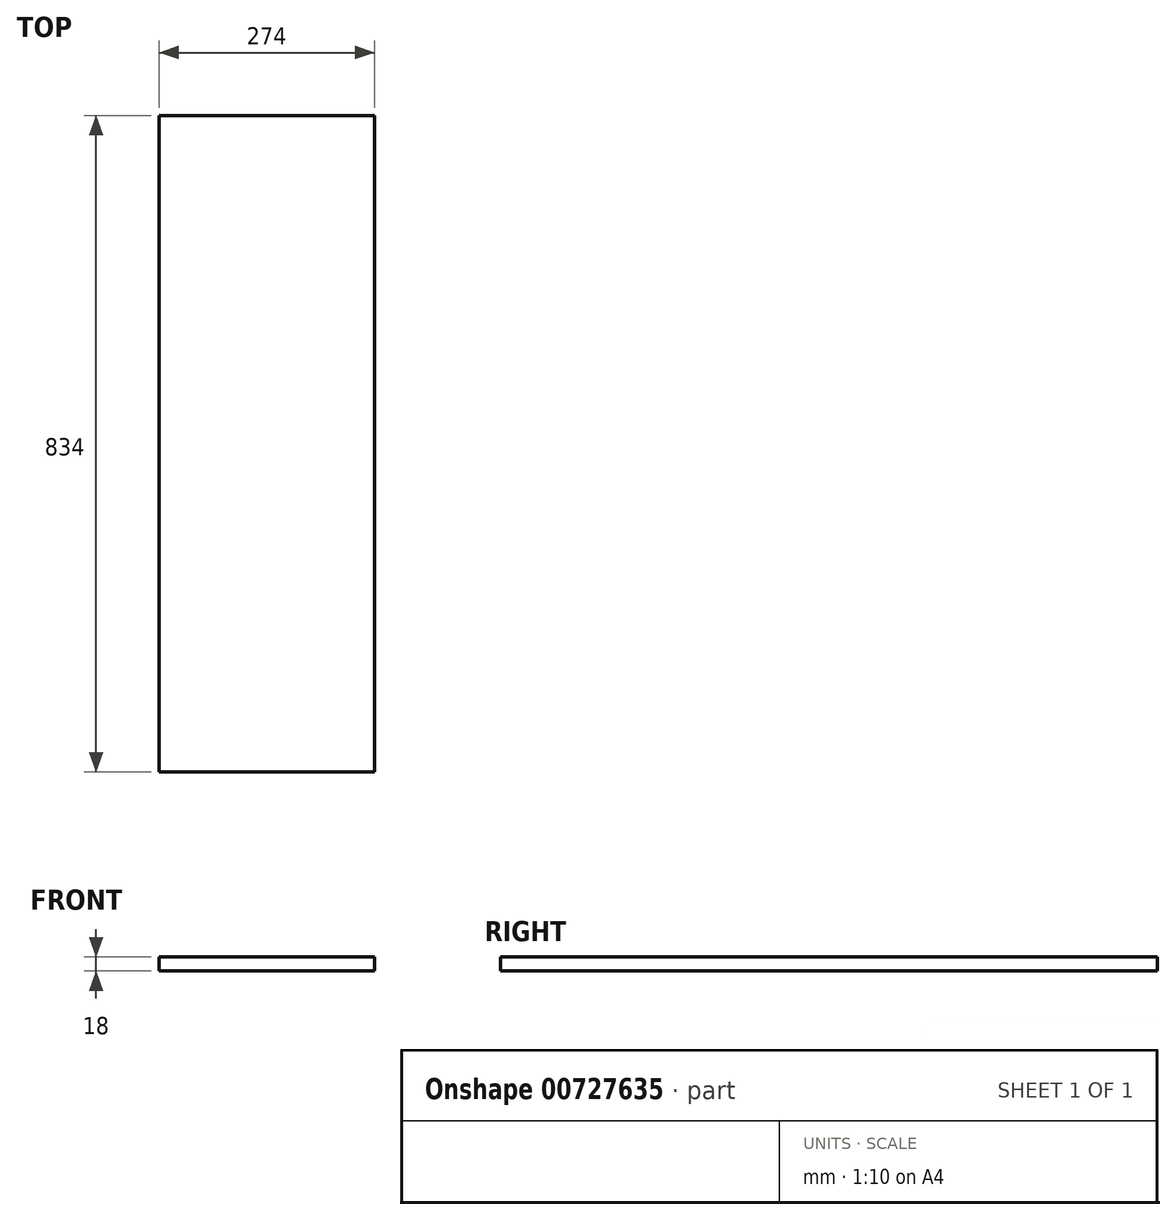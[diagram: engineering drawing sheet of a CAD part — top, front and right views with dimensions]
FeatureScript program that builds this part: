
annotation { "Feature Type Name" : "Feature", "Feature Type Description" : "" }
export const myFeature = defineFeature(function(context is Context, id is Id, definition is map)
    precondition{}
    {
        {
            var Q0;
            Q0=qCreatedBy(makeId("Top.planeOp"),FACE);
            var sketch = newSketch(context, id + "F0", { "sketchPlane" : qUnion([Q0])});
            skLineSegment(sketch, "E0.bottom", {"start": v(-137, -417) * mm, "end": v(137, -417) * mm});
            skLineSegment(sketch, "E0.top", {"start": v(-137, 417) * mm, "end": v(137, 417) * mm});
            skLineSegment(sketch, "E0.left", {"start": v(-137, -417) * mm, "end": v(-137, 417) * mm});
            skLineSegment(sketch, "E0.right", {"start": v(137, -417) * mm, "end": v(137, 417) * mm});
            skPoint(sketch, "E0.middle", {"position": v(0, 0) * mm});
            skSolve(sketch);
        }
        {
            var Q0;
            Q0 = qSketchRegion(id + "F0", true);
            extrude(context, id + "F1", {"entities" : qUnion([Q0]), "oppositeDirection" : true, "depth" : 18 * mm, "offsetDistance" : 25 * mm});
        }
    });
